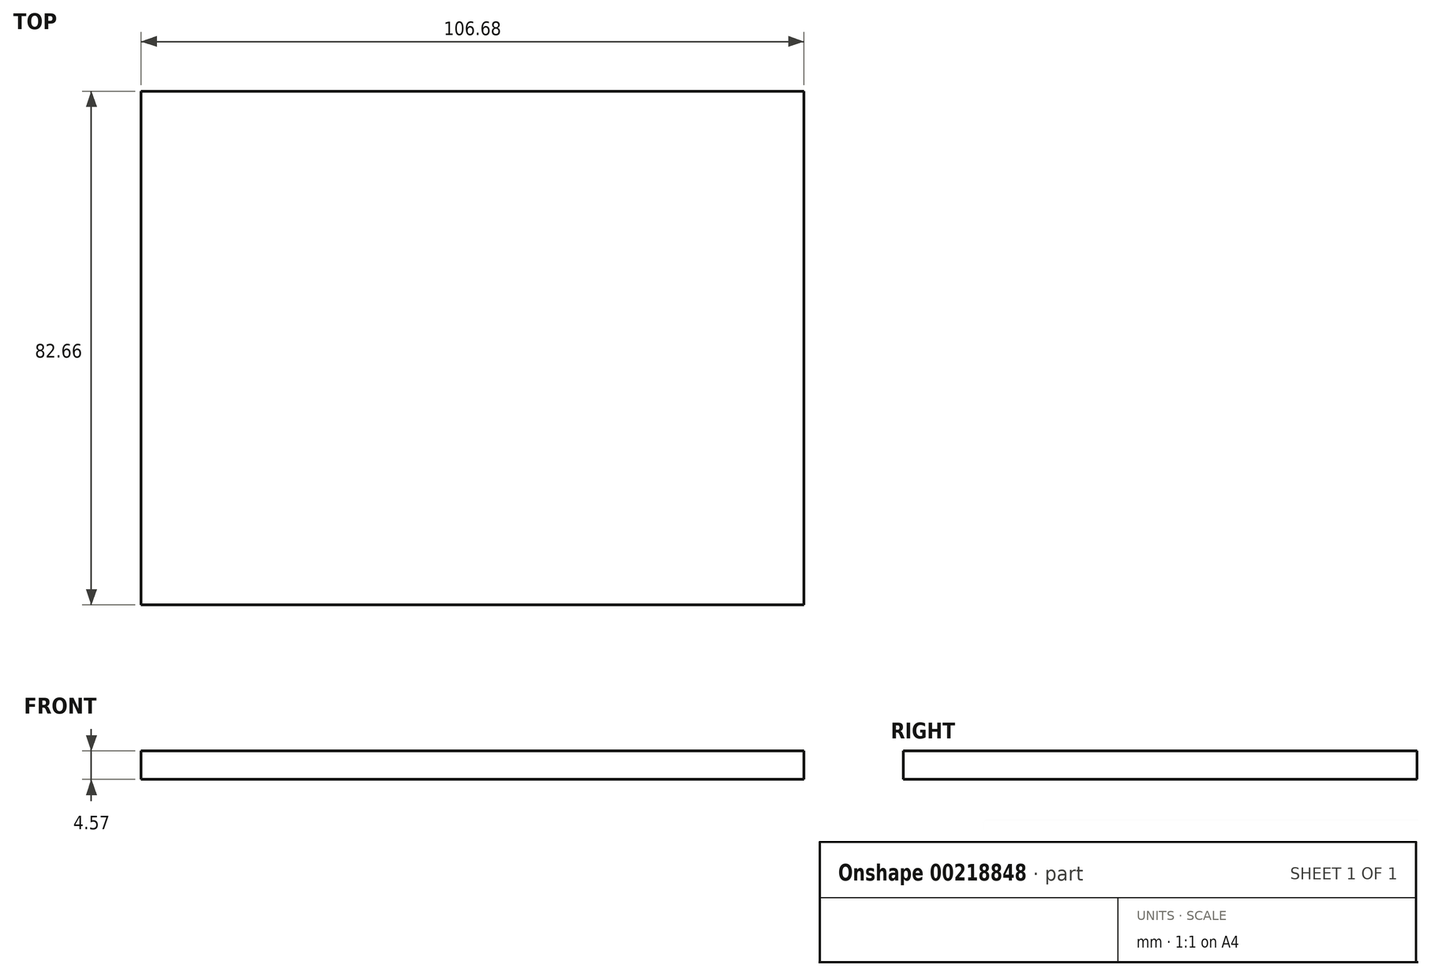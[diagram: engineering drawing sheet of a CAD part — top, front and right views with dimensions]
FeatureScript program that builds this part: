
annotation { "Feature Type Name" : "Feature", "Feature Type Description" : "" }
export const myFeature = defineFeature(function(context is Context, id is Id, definition is map)
    precondition{}
    {
        {
            var Q0;
            Q0=qCreatedBy(makeId("Top.planeOp"),FACE);
            var sketch = newSketch(context, id + "F0", { "sketchPlane" : qUnion([Q0])});
            skLineSegment(sketch, "E0.bottom", {"start": v(53.34, 41.33) * mm, "end": v(-53.34, 41.33) * mm});
            skLineSegment(sketch, "E0.top", {"start": v(53.34, -41.33) * mm, "end": v(-53.34, -41.33) * mm});
            skLineSegment(sketch, "E0.left", {"start": v(53.34, 41.33) * mm, "end": v(53.34, -41.33) * mm});
            skLineSegment(sketch, "E0.right", {"start": v(-53.34, 41.33) * mm, "end": v(-53.34, -41.33) * mm});
            skPoint(sketch, "E0.middle", {"position": v(0, 0) * mm});
            skSolve(sketch);
        }
        {
            var Q0;
            Q0=makeQuery(id+"F0.imprint","IMPRINT",FACE,{"disambiguationData":[TD([[makeQuery(id+"F0.imprint","IMPRINT",EDGE,{"derivedFrom":sQuery(id+"F0.wireOp",EDGE,"E0.bottom")}),1.0]])]});
            extrude(context, id + "F1", {"entities" : qUnion([Q0]), "depth" : 4.57 * mm});
        }
    });
